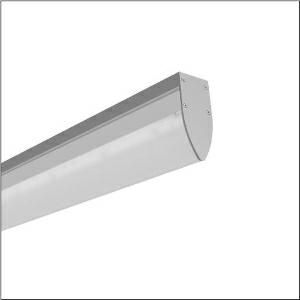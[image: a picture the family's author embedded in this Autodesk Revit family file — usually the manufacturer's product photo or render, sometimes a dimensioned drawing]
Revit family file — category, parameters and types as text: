
# Revit family: mira_r__21_td_51fr527p454a_1793
name_source: partatom
category: Lighting Fixtures
units: mm (PartAtom-declared; Revit-internal decimal feet)

## family parameters
Cut with Voids When Loaded = No
Host = Face
Light Source = No
Part Type = Normal
Room Calculation Point = No
Round Connector Dimension = Use Diameter
Shared = No

## types (1)
- Mira® 21 TD (1 x LED, 5040 lm, 34 W, 4000K)
    Apparent Load = 34 VA
    CIE Flux Codes = 40 68 87 81 100
    Color Rendering = 80
    Color Temperature = 4000K
    Default Elevation = 1800 mm
    Description = Mira® 21 TD, clean room luminaire, primary light control with reflector, primary optical cover: cover, of PMMA, frosted, light emission: direct distribution, primary light characteristic: symmetric, installation type: surface-mounted, LED, rated luminous flux: 5.040lm, luminous efficacy: 148lm/W, light colour: 840, colour temperature: 4000K, control gear: ON/OFF, with terminal, 3-pole, max. 2.5mm², mains connection: 230V, AC, 50/60Hz, rated input power: 34W, luminaire housing, of sheet steel, coated, pure white (RAL 9010), length: 1.500mm, width: 55mm, height: 120mm, protection rating (complete): IP43, insulation class (complete): insulation class I (protective earthing), certification: CE, UKCA, permissible operating ambient temperature: -5..+40°C, standard: EN 50419, packaging unit: 1 piece
    Height = 120 mm
    Lamp = 1 x LED
    Lamp Light Flux = 5040 lm
    Lamp Power = 34 W
    Lamp count = 1
    Length = 1500 mm
    Luminous efficacy = 148 lm/W
    Manufacturer = Siteco
    ModVariant = No
    Model = 51FR527P454A
    Mounting Place = Ceiling
    Mounting Type = Surface mounted
    Number of Poles = 1
    OnlyDefault = Yes
    Power Factor = 1
    Product Name = Mira® 21 TD
    Product group = clean room luminaire | ceiling mounted
    ProductGroupID = 305
    Protection Class = Protection class I
    Protection Degree = IP 43
    RLX_Detail_Level = 1
    RLX_Emergency_Light_Flux = 0 lm
    RLX_Emergency_Type = 0
    RLX_Emergency_Type_DB = No
    RlxData = <blob elided: 25173 chars, md5=546868b0>
    Socket = socket
    Standby Power = 0 W
    System Light Flux = 5040 lm
    System Power = 34 W
    Type Comments = Product without accessories
    Type Image = l_1007115.jpg
    URL = http://relux.com
    VarID = ---
    Voltage = 0 V
    Weight = 0.00 kg
    Width = 55 mm

## geometry (parser evidence)
native form markers: Blend x4, Sweep x13
no freeform markers — native parametric forms only
